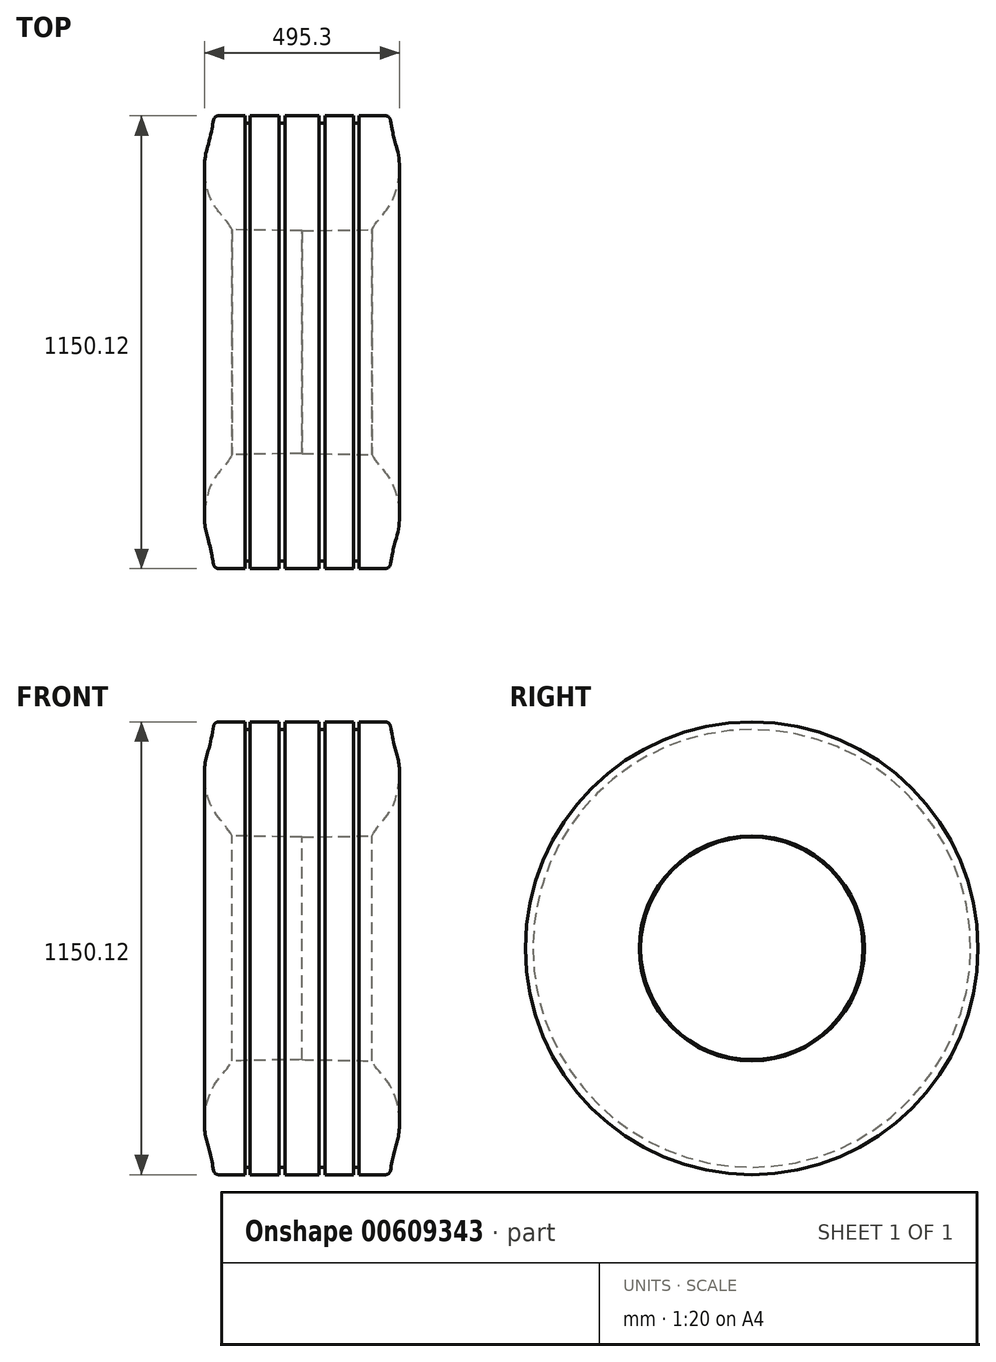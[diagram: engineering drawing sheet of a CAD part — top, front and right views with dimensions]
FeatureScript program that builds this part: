
annotation { "Feature Type Name" : "Feature", "Feature Type Description" : "" }
export const myFeature = defineFeature(function(context is Context, id is Id, definition is map)
    precondition{}
    {
        {
            var Q0;
            Q0=qCreatedBy(makeId("Front.planeOp"),FACE);
            var sketch = newSketch(context, id + "F0", { "sketchPlane" : qUnion([Q0])});
            skPoint(sketch, "E0", {"position": v(0, 0) * mm});
            skPoint(sketch, "E1", {"position": v(0, 575.06) * mm});
            skLineSegment(sketch, "E2", {"start": v(0, 575.06) * mm, "end": v(-212.1, 575.06) * mm});
            skPoint(sketch, "E3", {"position": v(-177.8, 285.75) * mm});
            skFitSpline(sketch, "E4", {"points": [v(-222.5, 575.06) * mm, v(-234.11, 517.2) * mm, v(-245.24, 474.56) * mm, v(-245.24, 412.44) * mm, v(-221.13, 344.76) * mm, v(-177.8, 285.75) * mm], "startDerivative": vector(-64.19, -305.01) * mm, "endDerivative": vector(157.54, -309.2) * mm});
            skArc(sketch, "E5.filletArc", {"start": v(-212.1, 575.06) * mm, "mid": v(-220.18, 572.15) * mm, "end": v(-224.57, 564.77) * mm});
            skLineSegment(sketch, "E6", {"start": v(0, 575.06) * mm, "end": v(0, 282.73) * mm});
            skLineSegment(sketch, "E7", {"start": v(0, 282.73) * mm, "end": v(-177.8, 285.75) * mm});
            skArc(sketch, "E8.MirrorCS", {"start": v(212.1, 575.06) * mm, "mid": v(220.18, 572.15) * mm, "end": v(224.57, 564.77) * mm});
            skPoint(sketch, "E9.MirrorP", {"position": v(177.8, 285.75) * mm});
            skLineSegment(sketch, "E10.MirrorCS", {"start": v(0, 575.06) * mm, "end": v(212.1, 575.06) * mm});
            skPoint(sketch, "E11.MirrorP", {"position": v(222.5, 575.06) * mm});
            skLineSegment(sketch, "E12.MirrorCS", {"start": v(0, 282.73) * mm, "end": v(177.8, 285.75) * mm});
            skFitSpline(sketch, "E13.MirrorCS", {"points": [v(222.5, 575.06) * mm, v(234.11, 517.2) * mm, v(245.24, 474.56) * mm, v(245.24, 412.44) * mm, v(221.13, 344.76) * mm, v(177.8, 285.75) * mm], "startDerivative": vector(64.19, -305.01) * mm, "endDerivative": vector(-157.54, -309.2) * mm});
            skLineSegment(sketch, "E14", {"start": v(0, 0) * mm, "end": v(-272.97, 0) * mm});
            skLineSegment(sketch, "E15.bottom", {"start": v(-144.93, 575.06) * mm, "end": v(-131.54, 575.06) * mm});
            skLineSegment(sketch, "E15.top", {"start": v(-144.93, 556) * mm, "end": v(-131.54, 556) * mm});
            skLineSegment(sketch, "E15.left", {"start": v(-144.93, 575.06) * mm, "end": v(-144.93, 556) * mm});
            skLineSegment(sketch, "E15.right", {"start": v(-131.54, 575.06) * mm, "end": v(-131.54, 556) * mm});
            skLineSegment(sketch, "E16.bottom", {"start": v(-58.85, 575.06) * mm, "end": v(-43.54, 575.06) * mm});
            skLineSegment(sketch, "E16.top", {"start": v(-58.85, 556) * mm, "end": v(-43.54, 556) * mm});
            skLineSegment(sketch, "E16.left", {"start": v(-58.85, 575.06) * mm, "end": v(-58.85, 556) * mm});
            skLineSegment(sketch, "E16.right", {"start": v(-43.54, 575.06) * mm, "end": v(-43.54, 556) * mm});
            skLineSegment(sketch, "E17.MirrorCS", {"start": v(58.85, 575.06) * mm, "end": v(58.85, 556) * mm});
            skLineSegment(sketch, "E18.MirrorCS", {"start": v(144.93, 575.06) * mm, "end": v(144.93, 556) * mm});
            skLineSegment(sketch, "E19.MirrorCS", {"start": v(144.93, 556) * mm, "end": v(131.54, 556) * mm});
            skLineSegment(sketch, "E20.MirrorCS", {"start": v(144.93, 575.06) * mm, "end": v(131.54, 575.06) * mm});
            skLineSegment(sketch, "E21.MirrorCS", {"start": v(58.85, 556) * mm, "end": v(43.54, 556) * mm});
            skLineSegment(sketch, "E22.MirrorCS", {"start": v(58.85, 575.06) * mm, "end": v(43.54, 575.06) * mm});
            skLineSegment(sketch, "E23.MirrorCS", {"start": v(131.54, 575.06) * mm, "end": v(131.54, 556) * mm});
            skLineSegment(sketch, "E24.MirrorCS", {"start": v(43.54, 575.06) * mm, "end": v(43.54, 556) * mm});
            skSolve(sketch);
        }
        {
            var Q0;
            Q0=makeQuery(id+"F0.imprint","IMPRINT",FACE,{"disambiguationData":[TD([[makeQuery(id+"F0.imprint","IMPRINT",EDGE,{"derivedFrom":sQuery(id+"F0.wireOp",EDGE,"E6")}),1.0]])]});
            var Q1;
            Q1=makeQuery(id+"F0.imprint","IMPRINT",FACE,{"disambiguationData":[TD([[makeQuery(id+"F0.imprint","IMPRINT",EDGE,{"derivedFrom":sQuery(id+"F0.wireOp",EDGE,"E4")}),1.0]])]});
            var Q2;
            Q2=sQuery(id+"F0.wireOp",EDGE,"E14");
            revolve(context, id + "F1", {"entities" : qUnion([Q0, Q1]), "axis" : qUnion([Q2]), "revolveType" : RevolveType.FULL});
        }
    });
